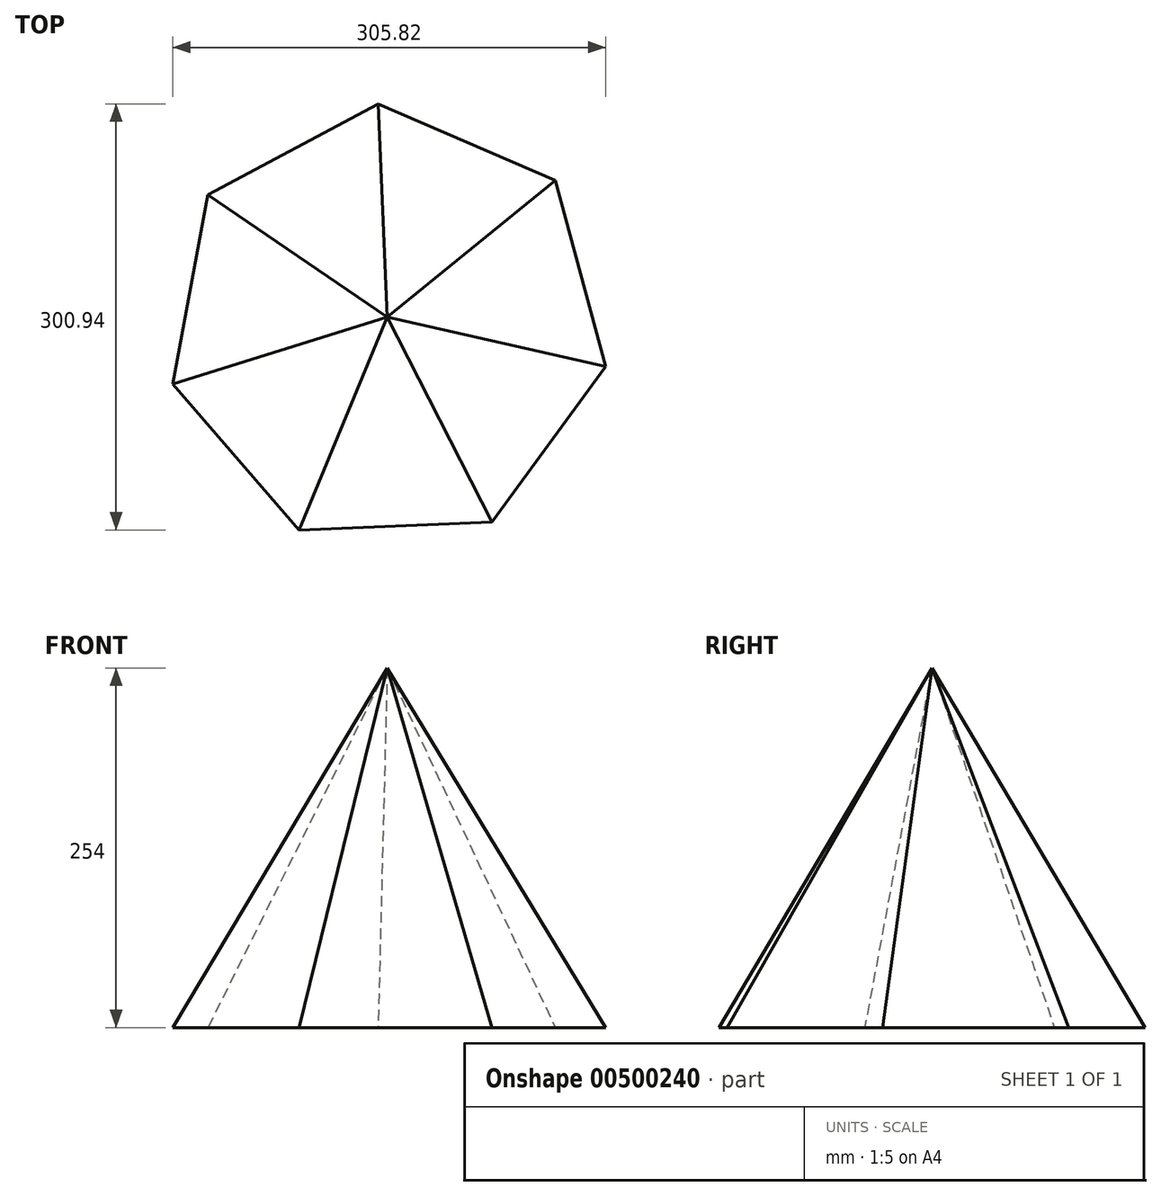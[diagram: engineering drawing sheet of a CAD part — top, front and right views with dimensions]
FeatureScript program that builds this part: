
annotation { "Feature Type Name" : "Feature", "Feature Type Description" : "" }
export const myFeature = defineFeature(function(context is Context, id is Id, definition is map)
    precondition{}
    {
        {
            var Q0;
            Q0=qCreatedBy(makeId("Top.planeOp"),FACE);
            var sketch = newSketch(context, id + "F0", { "sketchPlane" : qUnion([Q0])});
            skCircle(sketch, "E0.cCircle", {"center": v(0, 0) * mm, "radius": 156.97 * mm, "construction": true});
            skLineSegment(sketch, "E0.0", {"start": v(-151.48, -41.17) * mm, "end": v(-126.63, 92.76) * mm});
            skLineSegment(sketch, "E0.1", {"start": v(-126.63, 92.76) * mm, "end": v(-6.43, 156.84) * mm});
            skLineSegment(sketch, "E0.2", {"start": v(-6.43, 156.84) * mm, "end": v(118.61, 102.81) * mm});
            skLineSegment(sketch, "E0.3", {"start": v(118.61, 102.81) * mm, "end": v(154.34, -28.63) * mm});
            skLineSegment(sketch, "E0.4", {"start": v(154.34, -28.63) * mm, "end": v(73.84, -138.52) * mm});
            skLineSegment(sketch, "E0.5", {"start": v(73.84, -138.52) * mm, "end": v(-62.26, -144.1) * mm});
            skLineSegment(sketch, "E0.6", {"start": v(-62.26, -144.1) * mm, "end": v(-151.48, -41.17) * mm});
            skSolve(sketch);
        }
        {
            var Q0;
            Q0=qCreatedBy(makeId("Top.planeOp"),FACE);
            cPlane(context, id + "F1", {"entities" : qUnion([Q0]), "cplaneType" : CPlaneType.OFFSET, "offset" : 254 * mm, "width" : 150 * mm, "height" : 150 * mm});
        }
        {
            var Q0;
            Q0=qCreatedBy(id+"F1.planeOp",FACE);
            var sketch = newSketch(context, id + "F2", { "sketchPlane" : qUnion([Q0])});
            skPoint(sketch, "E1", {"position": v(0, 6.26) * mm});
            skSolve(sketch);
        }
        {
            var Q0;
            Q0=sQuery(id+"F2.wireOp",VERTEX,"E1");
            var Q1;
            Q1=makeQuery(id+"F0.imprint","IMPRINT",FACE,{"disambiguationData":[TD([[makeQuery(id+"F0.imprint","IMPRINT",EDGE,{"derivedFrom":sQuery(id+"F0.wireOp",EDGE,"E0.0")}),-1.0]])]});
            loft(context, id + "F3", {"sheetProfilesArray" : [{ "sheetProfileEntities" : qUnion([Q0]) }, { "sheetProfileEntities" : qUnion([Q1]) }]});
        }
    });
